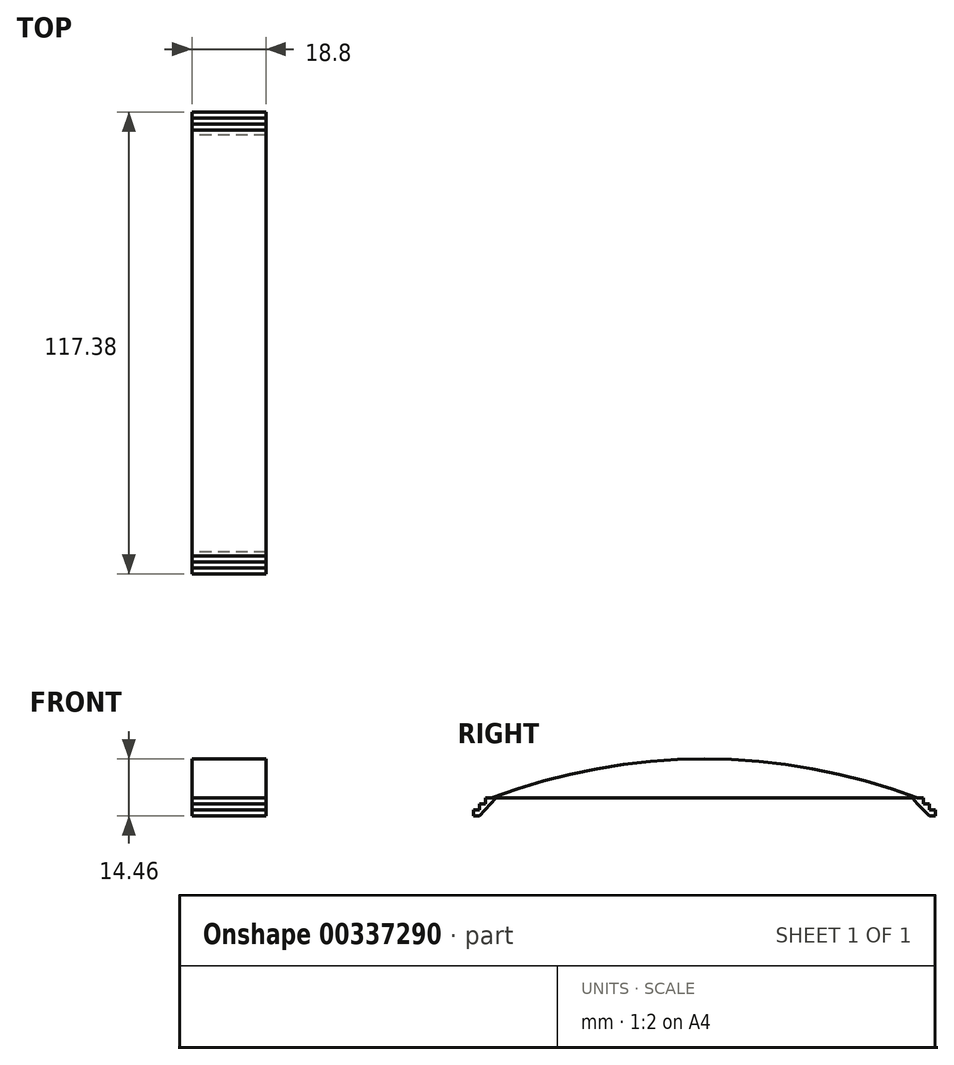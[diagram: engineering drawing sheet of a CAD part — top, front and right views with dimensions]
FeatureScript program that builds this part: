
annotation { "Feature Type Name" : "Feature", "Feature Type Description" : "" }
export const myFeature = defineFeature(function(context is Context, id is Id, definition is map)
    precondition{}
    {
        {
            var Q0;
            Q0=qCreatedBy(makeId("Right.planeOp"),FACE);
            var sketch = newSketch(context, id + "F0", { "sketchPlane" : qUnion([Q0])});
            skLineSegment(sketch, "E0", {"start": v(0, 0) * mm, "end": v(-54.1, 0) * mm});
            skLineSegment(sketch, "E1", {"start": v(-54.1, 0) * mm, "end": v(0, 0) * mm});
            skLineSegment(sketch, "E2", {"start": v(0, 0) * mm, "end": v(54.1, 0) * mm});
            skArc(sketch, "E3", {"start": v(54.1, 0) * mm, "mid": v(0, 9.86) * mm, "end": v(-54.1, 0) * mm});
            skLineSegment(sketch, "E4", {"start": v(-54.1, 0) * mm, "end": v(-55.64, 0) * mm});
            skLineSegment(sketch, "E5", {"start": v(-55.64, 0) * mm, "end": v(-55.64, -1.53) * mm});
            skLineSegment(sketch, "E6", {"start": v(-55.64, -1.53) * mm, "end": v(-57.18, -1.53) * mm});
            skLineSegment(sketch, "E7", {"start": v(-57.18, -1.53) * mm, "end": v(-57.18, -3.07) * mm});
            skLineSegment(sketch, "E8", {"start": v(-57.18, -3.07) * mm, "end": v(-58.71, -3.07) * mm});
            skLineSegment(sketch, "E9", {"start": v(-58.71, -3.07) * mm, "end": v(-58.71, -4.6) * mm});
            skLineSegment(sketch, "E10", {"start": v(-58.71, -4.6) * mm, "end": v(-57.18, -4.6) * mm});
            skLineSegment(sketch, "E11", {"start": v(-57.18, -4.6) * mm, "end": v(-53.05, 0) * mm});
            skLineSegment(sketch, "E12", {"start": v(54.1, 0) * mm, "end": v(55.63, 0) * mm});
            skLineSegment(sketch, "E13", {"start": v(55.63, 0) * mm, "end": v(55.63, -1.53) * mm});
            skLineSegment(sketch, "E14", {"start": v(55.63, -1.53) * mm, "end": v(57.15, -1.53) * mm});
            skLineSegment(sketch, "E15", {"start": v(57.15, -1.53) * mm, "end": v(57.15, -3.07) * mm});
            skLineSegment(sketch, "E16", {"start": v(57.15, -3.07) * mm, "end": v(58.67, -3.07) * mm});
            skLineSegment(sketch, "E17", {"start": v(58.67, -3.07) * mm, "end": v(58.67, -4.6) * mm});
            skLineSegment(sketch, "E18", {"start": v(58.67, -4.6) * mm, "end": v(57.15, -4.6) * mm});
            skLineSegment(sketch, "E19", {"start": v(57.15, -4.6) * mm, "end": v(54.1, -1.53) * mm});
            skLineSegment(sketch, "E20", {"start": v(54.1, -1.53) * mm, "end": v(52.76, 0) * mm});
            skSolve(sketch);
        }
        {
            var Q0;
            {var subQ0=sQuery(id+"F0.wireOp",EDGE,"E3");Q0=makeQuery(id+"F0.imprint","IMPRINT",FACE,{"disambiguationData":[TD([[makeQuery(id+"F0.imprint","IMPRINT",EDGE,{"derivedFrom":subQ0}),1.0]])]});}
            var Q1;
            {var subQ0=sQuery(id+"F0.wireOp",EDGE,"E4");Q1=makeQuery(id+"F0.imprint","IMPRINT",FACE,{"disambiguationData":[TD([[makeQuery(id+"F0.imprint","IMPRINT",EDGE,{"derivedFrom":subQ0}),1.0]])]});}
            var Q2;
            {var subQ0=sQuery(id+"F0.wireOp",EDGE,"E12");Q2=makeQuery(id+"F0.imprint","IMPRINT",FACE,{"disambiguationData":[TD([[makeQuery(id+"F0.imprint","IMPRINT",EDGE,{"derivedFrom":subQ0}),-1.0]])]});}
            extrude(context, id + "F1", {"entities" : qUnion([Q0, Q1, Q2]), "endBound" : BoundingType.SYMMETRIC, "depth" : 18.8 * mm});
        }
    });
